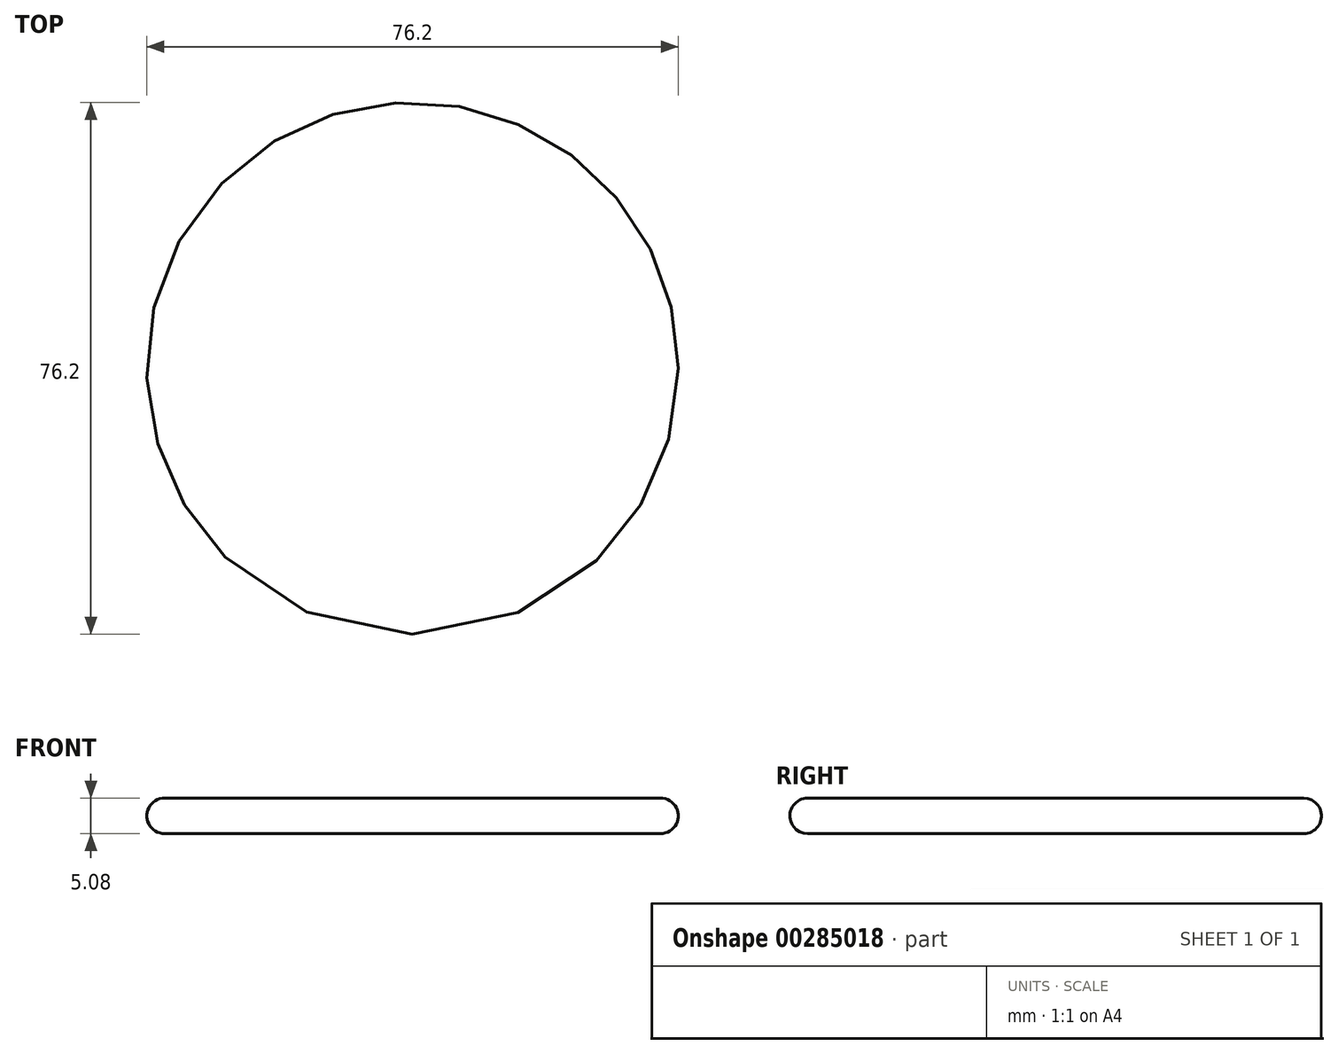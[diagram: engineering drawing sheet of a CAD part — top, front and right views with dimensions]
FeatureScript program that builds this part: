
annotation { "Feature Type Name" : "Feature", "Feature Type Description" : "" }
export const myFeature = defineFeature(function(context is Context, id is Id, definition is map)
    precondition{}
    {
        {
            var Q0;
            Q0=qCreatedBy(makeId("Top.planeOp"),FACE);
            var sketch = newSketch(context, id + "F0", { "sketchPlane" : qUnion([Q0])});
            skCircle(sketch, "E0", {"center": v(-59.42, 16.45) * mm, "radius": 38.1 * mm});
            skSolve(sketch);
        }
        {
            var Q0;
            Q0=makeQuery(id+"F0.imprint","IMPRINT",FACE,{"disambiguationData":[TD([[makeQuery(id+"F0.imprint","IMPRINT",EDGE,{"derivedFrom":sQuery(id+"F0.wireOp",EDGE,"E0")}),1.0]])]});
            extrude(context, id + "F1", {"entities" : qUnion([Q0]), "depth" : 5.08 * mm});
        }
        {
            var Q0;
            Q0=makeQuery(id+"F1.opExtrude","CAP_FACE",FACE,{"disambiguationData":[OSD([sQuery(id+"F0.wireOp",EDGE,"E0")])],"isStart":true});
            var Q1;
            Q1=makeQuery(id+"F1.opExtrude","CAP_EDGE",EDGE,{"disambiguationData":[OSD([sQuery(id+"F0.wireOp",EDGE,"E0")])],"isStart":false});
            fillet(context, id + "F2", {"entities" : qUnion([Q0, Q1]), "radius" : 2.54 * mm, "tangentPropagation" : true, "allowEdgeOverflow" : false});
        }
    });
